# Revit family: BRG-B+æR-CAB-PLATO DUCHA_ Rub+¡ Plato de ducha delgado
name_source: partatom
category: Modelos genéricos
units: mm (PartAtom-declared; Revit-internal decimal feet)

## family parameters
Anfitrión = Suelo
Compartido = No
Corte con vacíos al cargar = No
Cota de conector redondo = Diámetro de uso
Puede alojar armadura = No
Punto de cálculo de habitación = No
Siempre vertical = Sí
Tipo de pieza = Normal

## types (1)
- RUBÍ PLATO DE DUCHA DELGADO
    Elevación por defecto = 0 m
    Fabricante = BRIGGS
    Modelo = RUBÍ PLATO DE DUCHA DELGADO
    URL = https://www.briggs.com.ec
    _EDESA_ Alto en cm = 4.5
    _EDESA_ Ancho en cm = 120
    _EDESA_ Categoría = Productos > Bañeras > Cabinas de Ducha
    _EDESA_ Color = blanco
    _EDESA_ Conexión hidráulica = Salida de agua: tubería PVC 50
    _EDESA_ Descripción = Plato de ducha delgado.
    _EDESA_ Garantía = 1 año
    _EDESA_ Marca = BRIGGS
    _EDESA_ Materiales = Acrilico reforzado con fibra de vidrio con superficie antideslizante
    _EDESA_ Nombre = RUBÍ PLATO DE DUCHA DELGADO
    _EDESA_ Peso en kg = 17.0 kg
    _EDESA_ Productos incluídos = Desagüe
    _EDESA_ Productos necesarios para instalación = Sifón
    _EDESA_ Profundidad en cm = 80
    _EDESA_ Sku/código = SB0050671301M3
    _EDESA_ Tipo de instalación = Al piso
